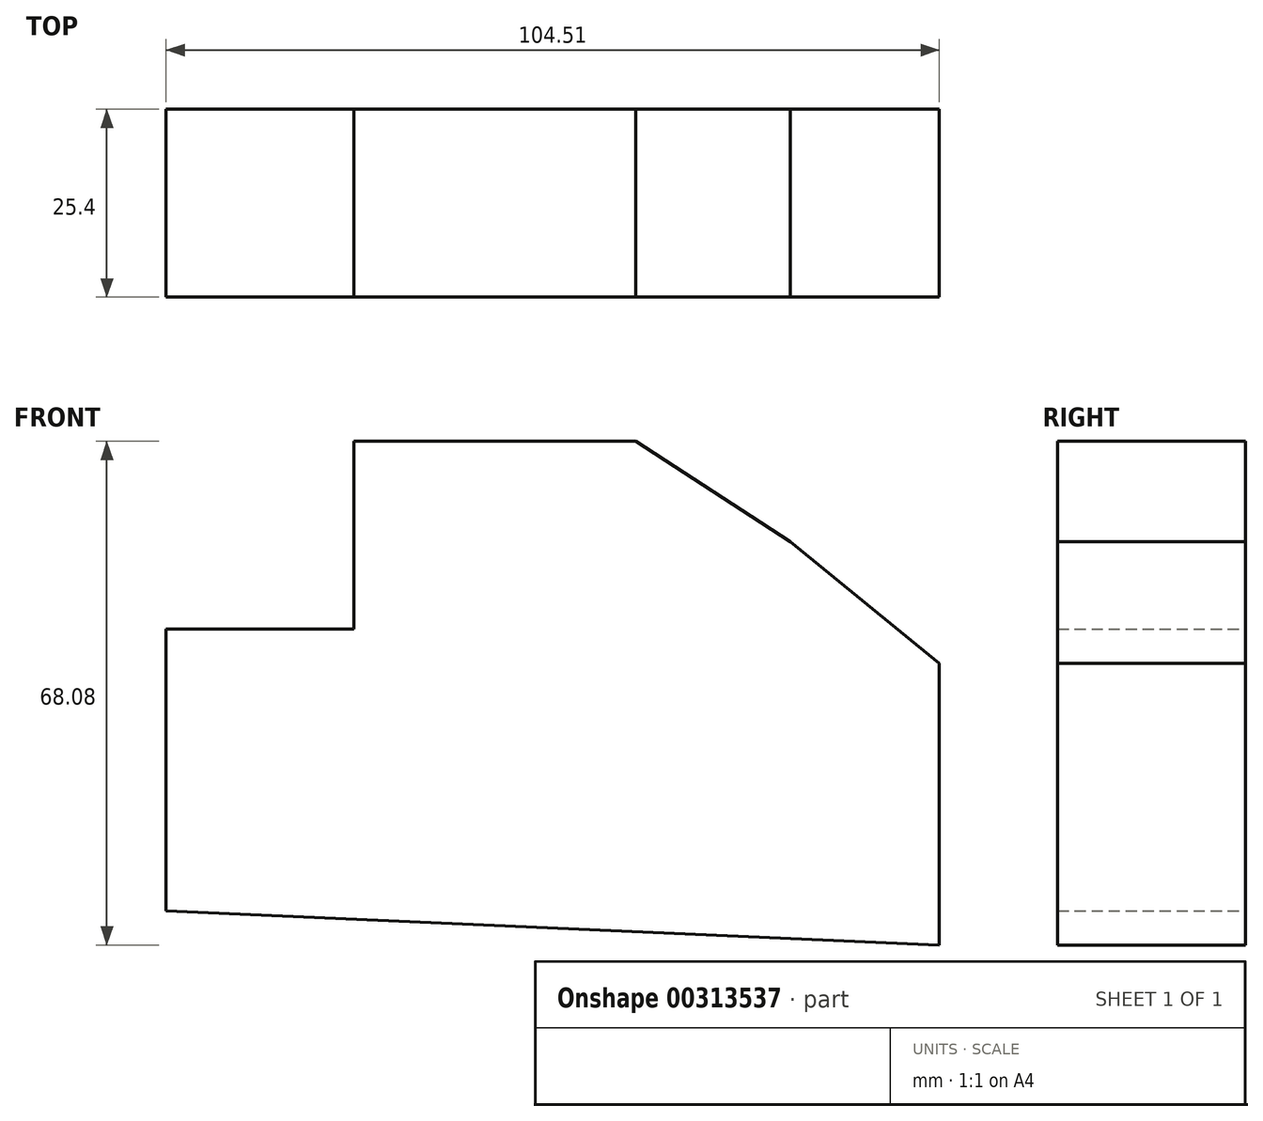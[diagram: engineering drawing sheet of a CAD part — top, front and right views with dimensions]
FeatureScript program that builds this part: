
annotation { "Feature Type Name" : "Feature", "Feature Type Description" : "" }
export const myFeature = defineFeature(function(context is Context, id is Id, definition is map)
    precondition{}
    {
        {
            var Q0;
            Q0=qCreatedBy(makeId("Front.planeOp"),FACE);
            var sketch = newSketch(context, id + "F0", { "sketchPlane" : qUnion([Q0])});
            skLineSegment(sketch, "E0", {"start": v(41.2, -26.2) * mm, "end": v(41.2, 11.9) * mm});
            skLineSegment(sketch, "E1", {"start": v(0.18, 41.9) * mm, "end": v(-37.92, 41.9) * mm});
            skLineSegment(sketch, "E2", {"start": v(-37.92, 41.9) * mm, "end": v(-37.92, 16.5) * mm});
            skLineSegment(sketch, "E3", {"start": v(-37.92, 16.5) * mm, "end": v(-63.32, 16.5) * mm});
            skLineSegment(sketch, "E4", {"start": v(-63.32, 16.5) * mm, "end": v(-63.32, -21.6) * mm});
            skLineSegment(sketch, "E5", {"start": v(-63.32, -21.6) * mm, "end": v(41.2, -26.2) * mm});
            skLineSegment(sketch, "E6", {"start": v(0.18, 41.9) * mm, "end": v(32.12, 21.12) * mm});
            skLineSegment(sketch, "E7", {"start": v(1.8, 44) * mm, "end": v(41.2, 11.9) * mm});
            skSolve(sketch);
        }
        {
            var Q0;
            Q0 = qSketchRegion(id + "F0", true);
            extrude(context, id + "F1", {"entities" : qUnion([Q0]), "depth" : 25.4 * mm});
        }
    });
